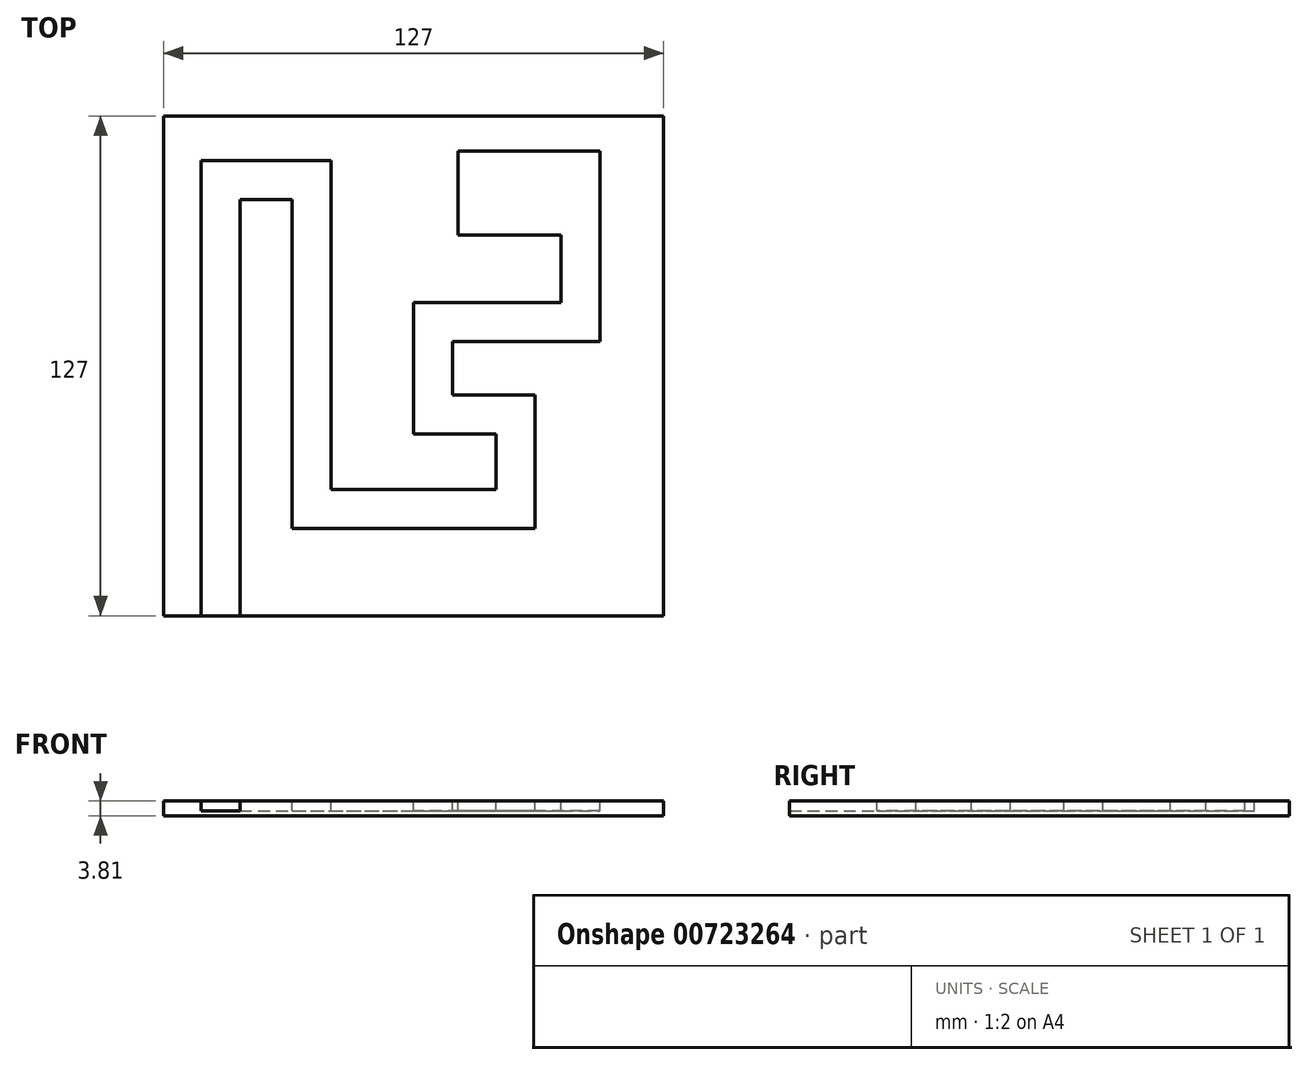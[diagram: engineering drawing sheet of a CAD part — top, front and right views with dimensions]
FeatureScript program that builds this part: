
annotation { "Feature Type Name" : "Feature", "Feature Type Description" : "" }
export const myFeature = defineFeature(function(context is Context, id is Id, definition is map)
    precondition{}
    {
        {
            var Q0;
            Q0=qCreatedBy(makeId("Top.planeOp"),FACE);
            var sketch = newSketch(context, id + "F0", { "sketchPlane" : qUnion([Q0])});
            skLineSegment(sketch, "E0.bottom", {"start": v(63.5, 63.5) * mm, "end": v(-63.5, 63.5) * mm});
            skLineSegment(sketch, "E0.top", {"start": v(63.5, -63.5) * mm, "end": v(-63.5, -63.5) * mm});
            skLineSegment(sketch, "E0.left", {"start": v(63.5, 63.5) * mm, "end": v(63.5, -63.5) * mm});
            skLineSegment(sketch, "E0.right", {"start": v(-63.5, 63.5) * mm, "end": v(-63.5, -63.5) * mm});
            skPoint(sketch, "E0.middle", {"position": v(0, 0) * mm});
            skSolve(sketch);
        }
        {
            var Q0;
            Q0=makeQuery(id+"F0.imprint","IMPRINT",FACE,{"disambiguationData":[TD([[makeQuery(id+"F0.imprint","IMPRINT",EDGE,{"derivedFrom":sQuery(id+"F0.wireOp",EDGE,"E0.bottom")}),1.0]])]});
            extrude(context, id + "F1", {"entities" : qUnion([Q0]), "depth" : 3.8 * mm, "offsetDistance" : 25.4 * mm});
        }
        {
            var Q0;
            Q0=makeQuery(id+"F1.opExtrude","CAP_FACE",FACE,{"disambiguationData":[OSD([sQuery(id+"F0.wireOp",EDGE,"E0.bottom"),sQuery(id+"F0.wireOp",EDGE,"E0.top"),sQuery(id+"F0.wireOp",EDGE,"E0.left"),sQuery(id+"F0.wireOp",EDGE,"E0.right")])],"isStart":false});
            var sketch = newSketch(context, id + "F2", { "sketchPlane" : qUnion([Q0])});
            skLineSegment(sketch, "E1", {"start": v(-54, -63.5) * mm, "end": v(-54, 52.19) * mm});
            skLineSegment(sketch, "E2", {"start": v(-54, 52.19) * mm, "end": v(-20.9, 52.19) * mm});
            skLineSegment(sketch, "E3", {"start": v(-20.9, 52.19) * mm, "end": v(-20.9, -31.43) * mm});
            skLineSegment(sketch, "E4", {"start": v(-20.9, -31.43) * mm, "end": v(20.9, -31.43) * mm});
            skLineSegment(sketch, "E5", {"start": v(20.9, -31.43) * mm, "end": v(20.9, -17.3) * mm});
            skLineSegment(sketch, "E6", {"start": v(20.9, -17.3) * mm, "end": v(0, -17.3) * mm});
            skLineSegment(sketch, "E7", {"start": v(0, -17.3) * mm, "end": v(0, 16.1) * mm});
            skLineSegment(sketch, "E8", {"start": v(0, 16.1) * mm, "end": v(37.45, 16.1) * mm});
            skLineSegment(sketch, "E9", {"start": v(37.45, 16.1) * mm, "end": v(37.45, 33.24) * mm});
            skLineSegment(sketch, "E10.0", {"start": v(47.35, 6.19) * mm, "end": v(47.35, 33.24) * mm});
            skLineSegment(sketch, "E10.1", {"start": v(9.9, 6.19) * mm, "end": v(47.35, 6.19) * mm});
            skLineSegment(sketch, "E10.2", {"start": v(9.9, -7.39) * mm, "end": v(9.9, 6.19) * mm});
            skLineSegment(sketch, "E10.3", {"start": v(30.81, -7.39) * mm, "end": v(9.9, -7.39) * mm});
            skLineSegment(sketch, "E10.4", {"start": v(30.81, -41.34) * mm, "end": v(30.81, -7.39) * mm});
            skLineSegment(sketch, "E10.5", {"start": v(-44.09, -63.5) * mm, "end": v(-44.09, 42.28) * mm});
            skLineSegment(sketch, "E10.6", {"start": v(-44.09, 42.28) * mm, "end": v(-30.81, 42.28) * mm});
            skLineSegment(sketch, "E10.7", {"start": v(-30.81, 42.28) * mm, "end": v(-30.81, -41.34) * mm});
            skLineSegment(sketch, "E10.8", {"start": v(-30.81, -41.34) * mm, "end": v(30.81, -41.34) * mm});
            skLineSegment(sketch, "E11", {"start": v(37.45, 33.24) * mm, "end": v(47.35, 33.24) * mm});
            skLineSegment(sketch, "E12", {"start": v(-54, -63.5) * mm, "end": v(-44.09, -63.5) * mm});
            skSolve(sketch);
        }
        {
            var Q0;
            Q0=makeQuery(id+"F2.imprint","IMPRINT",FACE,{"disambiguationData":[TD([[makeQuery(id+"F2.imprint","IMPRINT",EDGE,{"derivedFrom":sQuery(id+"F2.wireOp",EDGE,"E1")}),-1.0]])]});
            extrude(context, id + "F3", {"entities" : qUnion([Q0]), "operationType" : NewBodyOperationType.REMOVE, "oppositeDirection" : true, "depth" : 2.54 * mm, "offsetDistance" : 25.4 * mm});
        }
        {
            var Q0;
            Q0=makeQuery(id+"F1.opExtrude","CAP_FACE",FACE,{"disambiguationData":[OSD([sQuery(id+"F0.wireOp",EDGE,"E0.bottom"),sQuery(id+"F0.wireOp",EDGE,"E0.top"),sQuery(id+"F0.wireOp",EDGE,"E0.left"),sQuery(id+"F0.wireOp",EDGE,"E0.right")])],"isStart":false});
            var sketch = newSketch(context, id + "F4", { "sketchPlane" : qUnion([Q0])});
            skLineSegment(sketch, "E13.bottom", {"start": v(47.35, 33.24) * mm, "end": v(11.28, 33.24) * mm});
            skLineSegment(sketch, "E13.top", {"start": v(47.35, 54.6) * mm, "end": v(11.28, 54.6) * mm});
            skLineSegment(sketch, "E13.left", {"start": v(47.35, 33.24) * mm, "end": v(47.35, 54.6) * mm});
            skLineSegment(sketch, "E13.right", {"start": v(11.28, 33.24) * mm, "end": v(11.28, 54.6) * mm});
            skSolve(sketch);
        }
        {
            var Q0;
            Q0=makeQuery(id+"F4.imprint","IMPRINT",FACE,{"disambiguationData":[TD([[makeQuery(id+"F4.imprint","IMPRINT",EDGE,{"derivedFrom":sQuery(id+"F4.wireOp",EDGE,"E13.top")}),1.0]])]});
            extrude(context, id + "F5", {"entities" : qUnion([Q0]), "operationType" : NewBodyOperationType.REMOVE, "oppositeDirection" : true, "depth" : 2.54 * mm, "offsetDistance" : 25.4 * mm});
        }
    });
